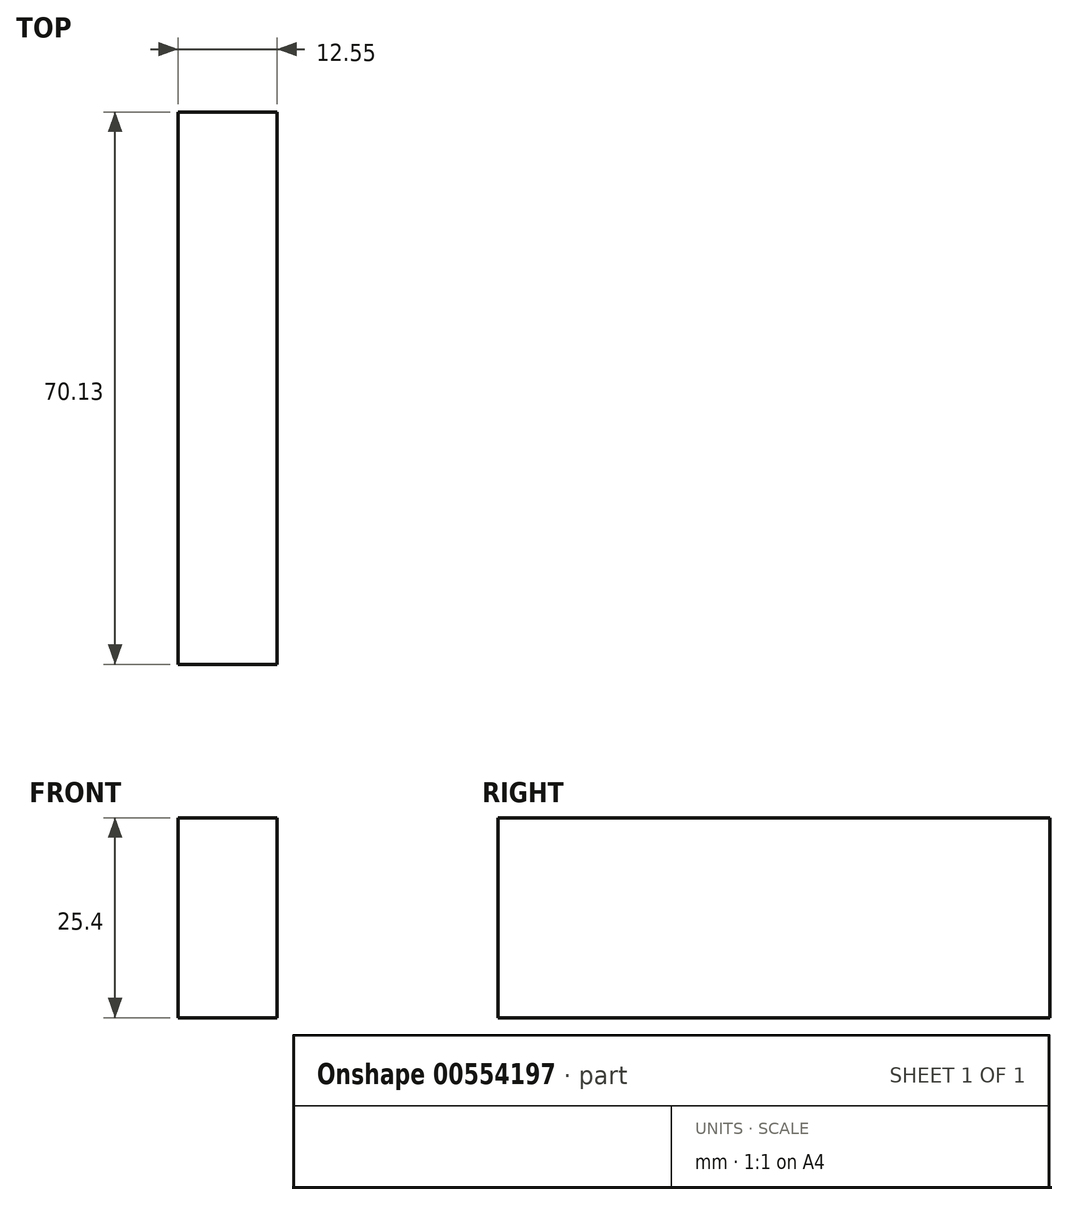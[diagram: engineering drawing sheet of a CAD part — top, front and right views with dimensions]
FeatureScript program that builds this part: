
annotation { "Feature Type Name" : "Feature", "Feature Type Description" : "" }
export const myFeature = defineFeature(function(context is Context, id is Id, definition is map)
    precondition{}
    {
        {
            var Q0;
            Q0=qCreatedBy(makeId("Top.planeOp"),FACE);
            var sketch = newSketch(context, id + "F0", { "sketchPlane" : qUnion([Q0])});
            skLineSegment(sketch, "E0.bottom", {"start": v(0, 70.13) * mm, "end": v(12.55, 70.13) * mm});
            skLineSegment(sketch, "E0.top", {"start": v(0, 0) * mm, "end": v(12.55, 0) * mm});
            skLineSegment(sketch, "E0.left", {"start": v(0, 70.13) * mm, "end": v(0, 0) * mm});
            skLineSegment(sketch, "E0.right", {"start": v(12.55, 70.13) * mm, "end": v(12.55, 0) * mm});
            skSolve(sketch);
        }
        {
            var Q0;
            Q0 = qSketchRegion(id + "F0", true);
            extrude(context, id + "F1", {"entities" : qUnion([Q0]), "depth" : 25.4 * mm, "offsetDistance" : 25.4 * mm});
        }
    });
